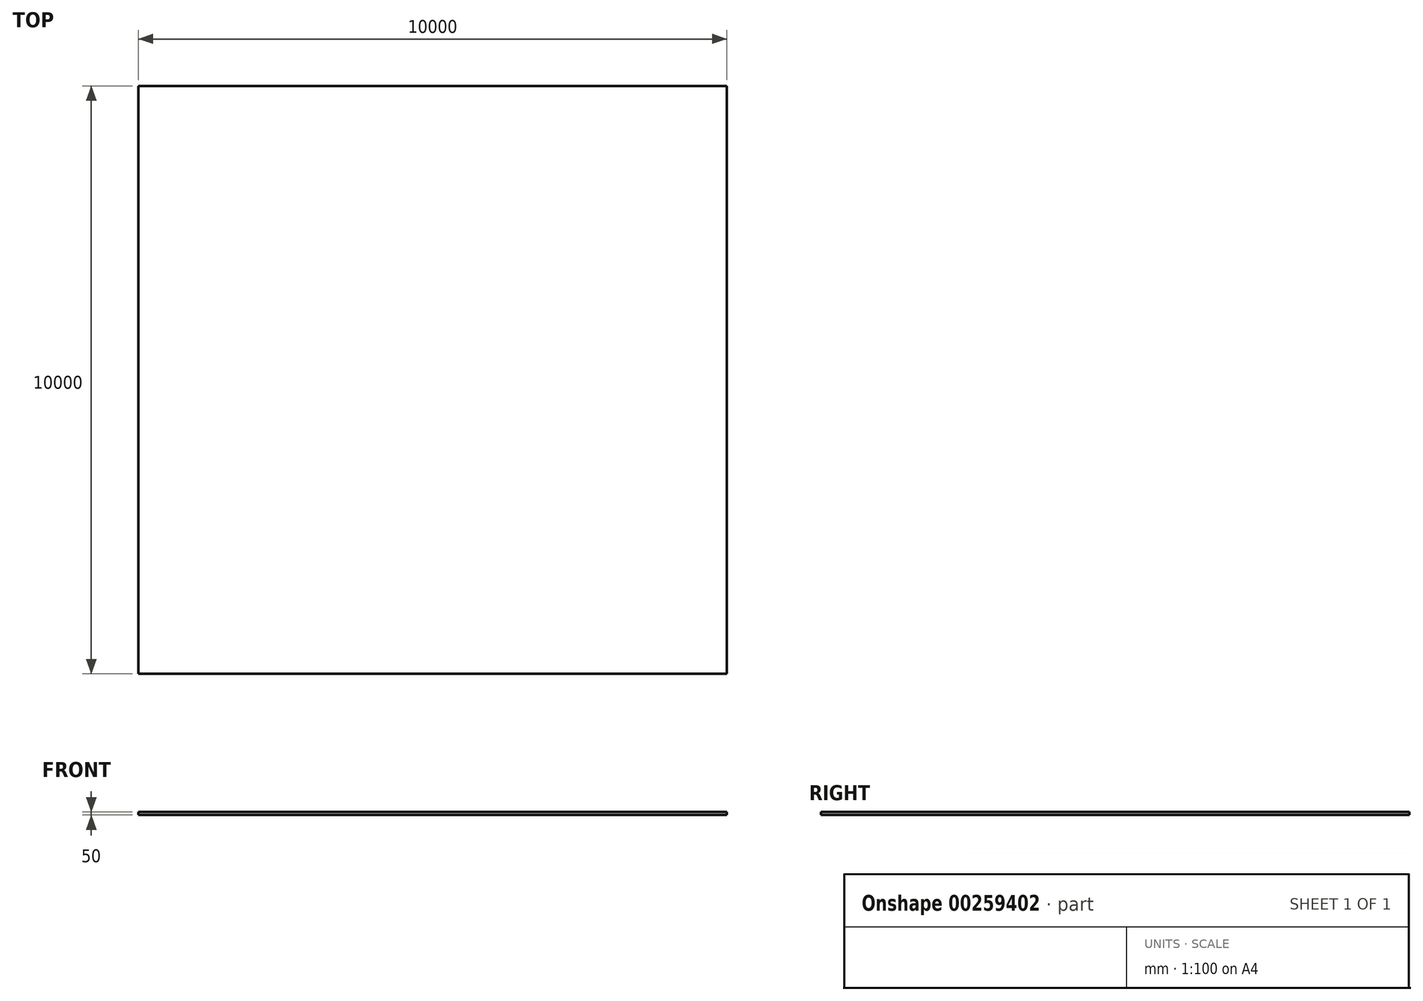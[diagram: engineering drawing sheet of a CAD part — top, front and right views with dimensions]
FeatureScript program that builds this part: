
annotation { "Feature Type Name" : "Feature", "Feature Type Description" : "" }
export const myFeature = defineFeature(function(context is Context, id is Id, definition is map)
    precondition{}
    {
        {
            var Q0;
            Q0=qCreatedBy(makeId("Top.planeOp"),FACE);
            var sketch = newSketch(context, id + "F0", { "sketchPlane" : qUnion([Q0])});
            skLineSegment(sketch, "E0.bottom", {"start": v(5000, 5000) * mm, "end": v(-5000, 5000) * mm});
            skLineSegment(sketch, "E0.top", {"start": v(5000, -5000) * mm, "end": v(-5000, -5000) * mm});
            skLineSegment(sketch, "E0.left", {"start": v(5000, 5000) * mm, "end": v(5000, -5000) * mm});
            skLineSegment(sketch, "E0.right", {"start": v(-5000, 5000) * mm, "end": v(-5000, -5000) * mm});
            skPoint(sketch, "E0.middle", {"position": v(0, 0) * mm});
            skSolve(sketch);
        }
        {
            var Q0;
            Q0=makeQuery(id+"F0.imprint","IMPRINT",FACE,{"disambiguationData":[TD([[makeQuery(id+"F0.imprint","IMPRINT",EDGE,{"derivedFrom":sQuery(id+"F0.wireOp",EDGE,"E0.bottom")}),1.0]])]});
            extrude(context, id + "F1", {"entities" : qUnion([Q0]), "depth" : 50 * mm});
        }
    });
